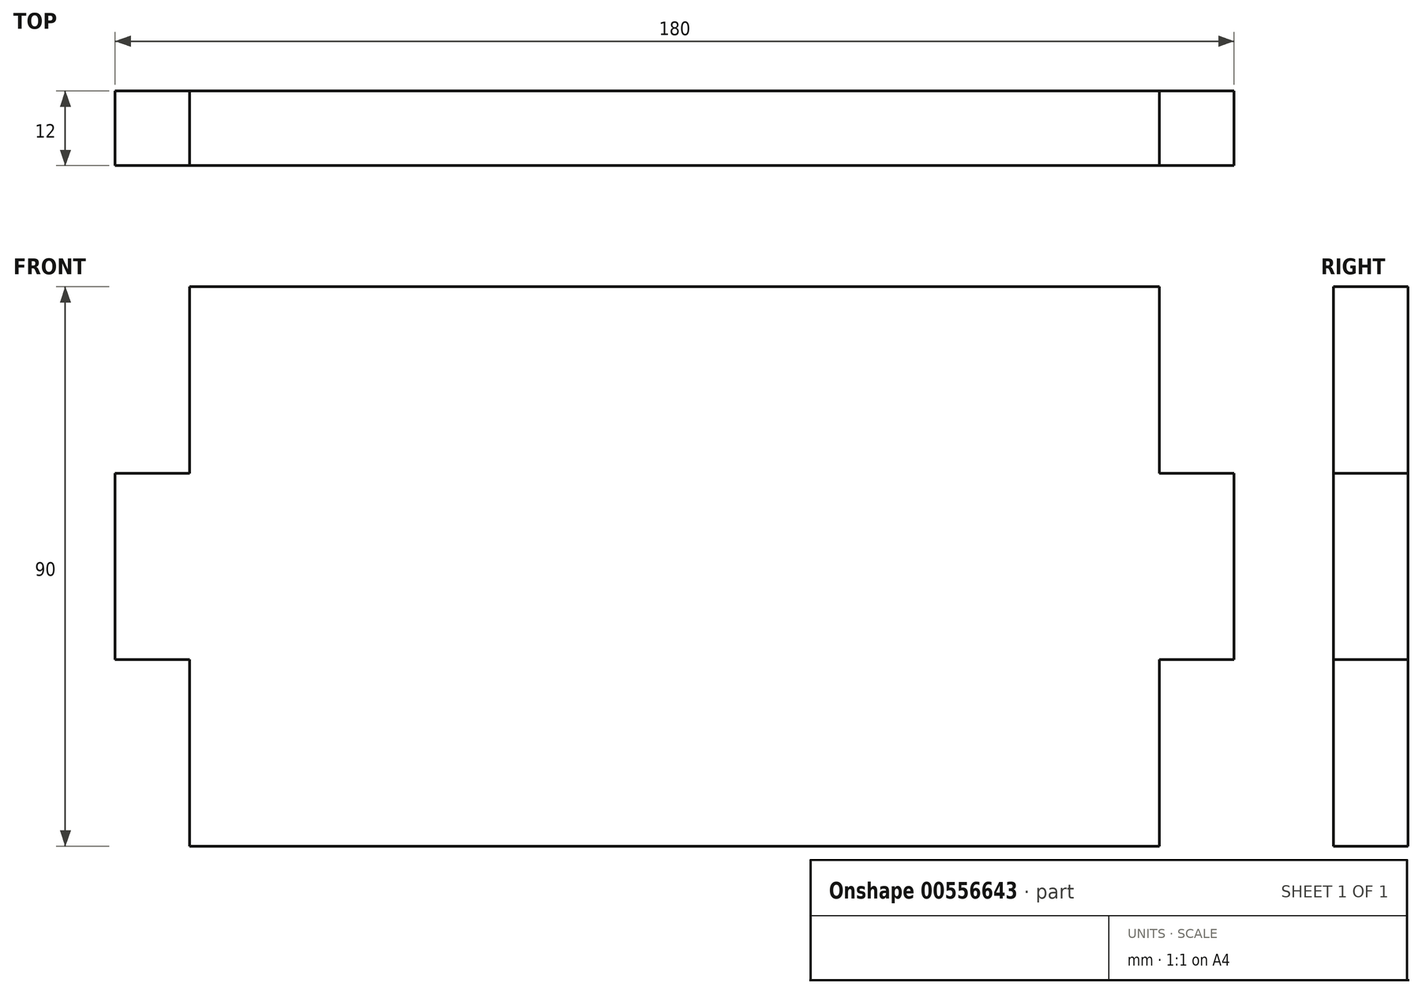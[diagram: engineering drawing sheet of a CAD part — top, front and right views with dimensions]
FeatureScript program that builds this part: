
annotation { "Feature Type Name" : "Feature", "Feature Type Description" : "" }
export const myFeature = defineFeature(function(context is Context, id is Id, definition is map)
    precondition{}
    {
        {
            var Q0;
            Q0=qCreatedBy(makeId("Front.planeOp"),FACE);
            var sketch = newSketch(context, id + "F0", { "sketchPlane" : qUnion([Q0])});
            skLineSegment(sketch, "E0", {"start": v(0, 0) * mm, "end": v(0, 30) * mm});
            skLineSegment(sketch, "E1", {"start": v(0, 30) * mm, "end": v(-12, 30) * mm});
            skLineSegment(sketch, "E2", {"start": v(-12, 30) * mm, "end": v(-12, 60) * mm});
            skLineSegment(sketch, "E3", {"start": v(-12, 60) * mm, "end": v(0, 60) * mm});
            skLineSegment(sketch, "E4", {"start": v(0, 60) * mm, "end": v(0, 90) * mm});
            skLineSegment(sketch, "E5", {"start": v(0, 90) * mm, "end": v(78, 90) * mm});
            skLineSegment(sketch, "E6", {"start": v(78, 90) * mm, "end": v(78, 0) * mm, "construction": true});
            skLineSegment(sketch, "E7", {"start": v(78, 0) * mm, "end": v(0, 0) * mm});
            skLineSegment(sketch, "E8.MirrorCS", {"start": v(156, 30) * mm, "end": v(168, 30) * mm});
            skLineSegment(sketch, "E9.MirrorCS", {"start": v(168, 30) * mm, "end": v(168, 60) * mm});
            skLineSegment(sketch, "E10.MirrorCS", {"start": v(156, 60) * mm, "end": v(156, 90) * mm});
            skLineSegment(sketch, "E11.MirrorCS", {"start": v(156, 0) * mm, "end": v(156, 30) * mm});
            skLineSegment(sketch, "E12.MirrorCS", {"start": v(156, 90) * mm, "end": v(78, 90) * mm});
            skLineSegment(sketch, "E13.MirrorCS", {"start": v(168, 60) * mm, "end": v(156, 60) * mm});
            skLineSegment(sketch, "E14.MirrorCS", {"start": v(78, 0) * mm, "end": v(156, 0) * mm});
            skSolve(sketch);
        }
        {
            var Q0;
            Q0=makeQuery(id+"F0.imprint","IMPRINT",FACE,{"disambiguationData":[TD([[makeQuery(id+"F0.imprint","IMPRINT",EDGE,{"derivedFrom":sQuery(id+"F0.wireOp",EDGE,"E0")}),-1.0]])]});
            extrude(context, id + "F1", {"entities" : qUnion([Q0]), "depth" : 12 * mm, "offsetDistance" : 25 * mm});
        }
    });
